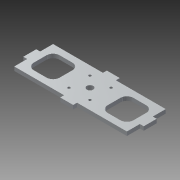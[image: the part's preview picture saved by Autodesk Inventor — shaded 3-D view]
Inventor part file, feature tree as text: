
AUTODESK INVENTOR PART (.ipt)
format: ipt  version: 2013 (Build 170138000, 138)  size: 161,280 bytes
history: native  units: mm
features: extrude x1, sketch x1
ambient origin geometry x8: Origin, YZ Plane, XZ Plane, XY Plane, X Axis, Y Axis, Z Axis, Center Point
bodies: Solid1 (feature_tree)
feature tree (2):
  extrude  "Extrusion1"  Depth=10.0mm
  sketch  "Sketch1"  dims[d0=10.0mm d1=10.0mm d2=10.0mm d3=10.0mm d4=10.0mm d5=10.0mm d6=38.5mm d7=38.5mm d8=10.0mm d9=38.5mm d11=38.5mm d12=5.0mm d13=5.0mm d15=5.0mm d16=20.0mm d17=5.0mm d18=5.0mm d19=5.0mm d20=20.0mm d21=3.0mm d23=3.0mm d24=3.0mm d25=5.0mm d26=5.0mm d27=5.0mm d28=15.0mm d30=2.0mm d32=40.0mm d34=360.0deg d36=3.0mm d37=0.0mm d38=3.0mm d39=10.0mm]
